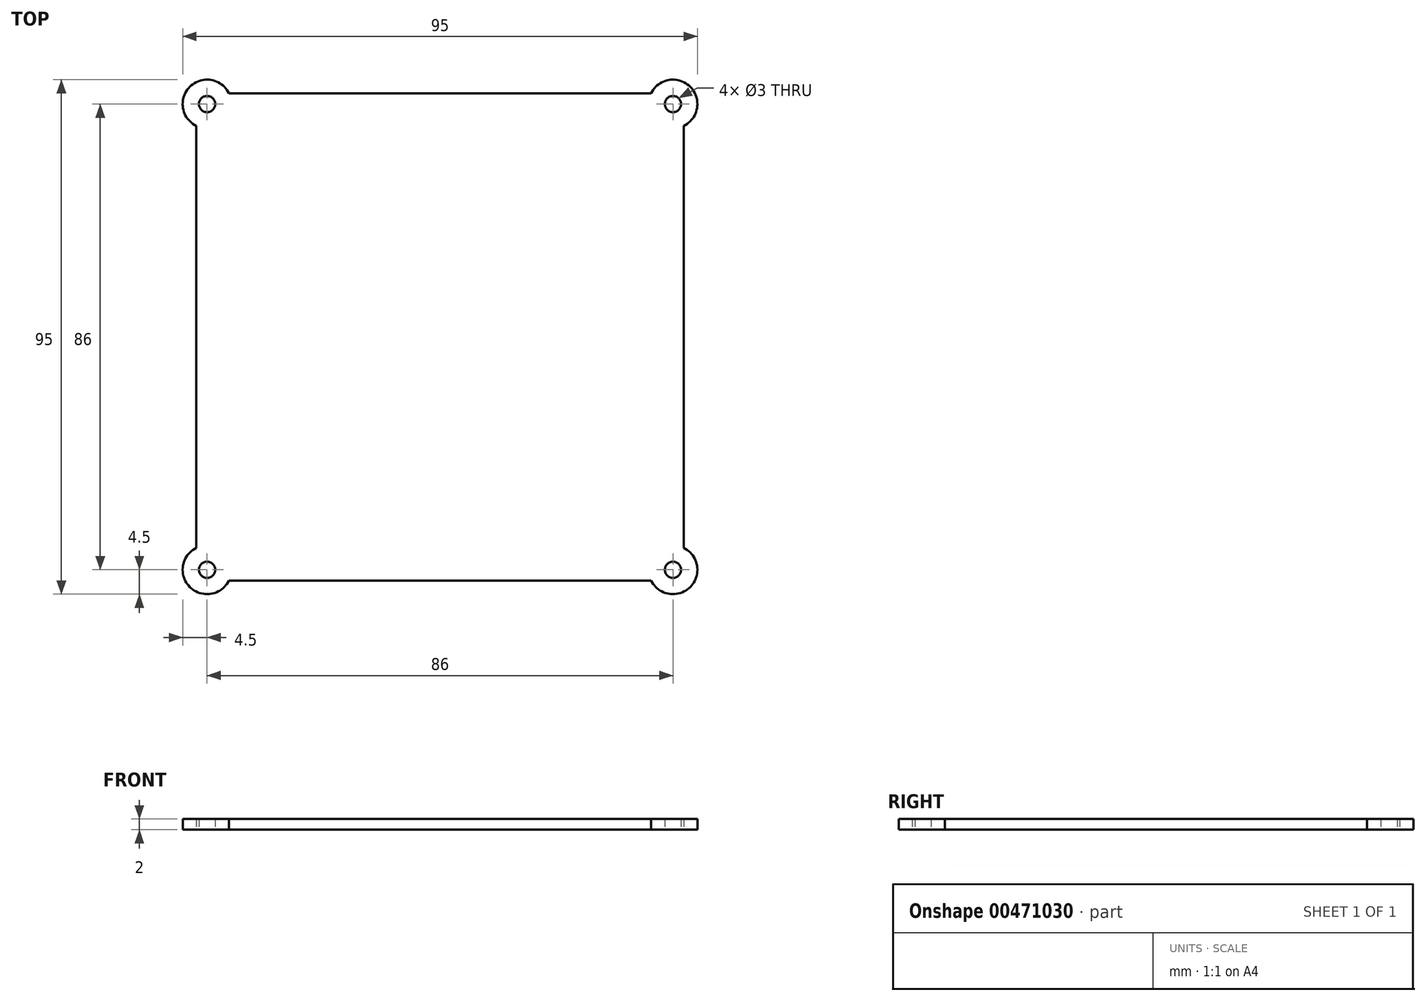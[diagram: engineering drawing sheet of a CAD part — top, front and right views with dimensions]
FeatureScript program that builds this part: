
annotation { "Feature Type Name" : "Feature", "Feature Type Description" : "" }
export const myFeature = defineFeature(function(context is Context, id is Id, definition is map)
    precondition{}
    {
        {
            var Q0;
            Q0=qCreatedBy(makeId("Top.planeOp"),FACE);
            var sketch = newSketch(context, id + "F0", { "sketchPlane" : qUnion([Q0])});
            skLineSegment(sketch, "E0.bottom", {"start": v(2, 88) * mm, "end": v(88, 88) * mm, "construction": true});
            skLineSegment(sketch, "E0.left", {"start": v(2, 88) * mm, "end": v(2, 2) * mm, "construction": true});
            skLineSegment(sketch, "E0.right", {"start": v(88, 88) * mm, "end": v(88, 2) * mm, "construction": true});
            skArc(sketch, "E1", {"start": v(6.03, 90) * mm, "mid": v(-1.18, 91.18) * mm, "end": v(0, 83.97) * mm});
            skArc(sketch, "E2", {"start": v(90, 83.97) * mm, "mid": v(91.18, 91.18) * mm, "end": v(83.97, 90) * mm});
            skArc(sketch, "E3", {"start": v(0, 6.03) * mm, "mid": v(-1.18, -1.18) * mm, "end": v(6.03, 0) * mm});
            skArc(sketch, "E4", {"start": v(83.97, 0) * mm, "mid": v(91.18, -1.18) * mm, "end": v(90, 6.03) * mm});
            skLineSegment(sketch, "E5.bottom", {"start": v(6.03, 0) * mm, "end": v(83.97, 0) * mm});
            skLineSegment(sketch, "E5.top", {"start": v(6.03, 90) * mm, "end": v(83.97, 90) * mm});
            skLineSegment(sketch, "E5.left", {"start": v(0, 6.03) * mm, "end": v(0, 83.97) * mm});
            skLineSegment(sketch, "E5.right", {"start": v(90, 6.03) * mm, "end": v(90, 83.97) * mm});
            skLineSegment(sketch, "E6", {"start": v(2, 2) * mm, "end": v(88, 2) * mm, "construction": true});
            skCircle(sketch, "E7", {"center": v(2, 2) * mm, "radius": 1.5 * mm});
            skCircle(sketch, "E8", {"center": v(88, 2) * mm, "radius": 1.5 * mm});
            skCircle(sketch, "E9", {"center": v(2, 88) * mm, "radius": 1.5 * mm});
            skCircle(sketch, "E10", {"center": v(88, 88) * mm, "radius": 1.5 * mm});
            skSolve(sketch);
        }
        {
            var Q0;
            Q0 = qSketchRegion(id + "F0", true);
            extrude(context, id + "F1", {"entities" : qUnion([Q0]), "depth" : 2 * mm});
        }
    });
